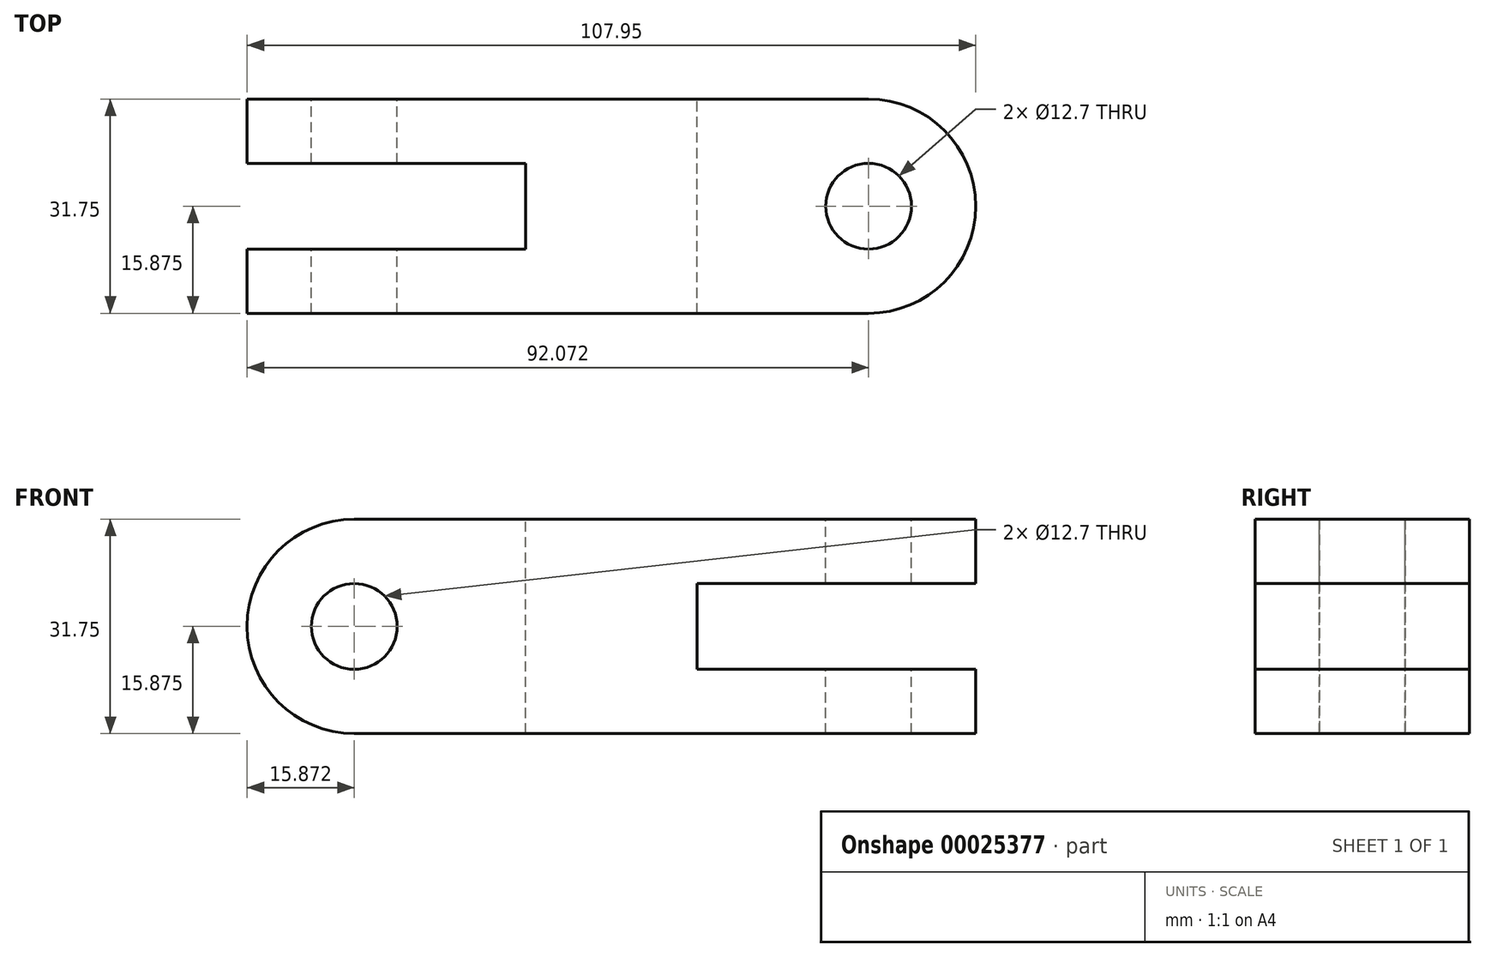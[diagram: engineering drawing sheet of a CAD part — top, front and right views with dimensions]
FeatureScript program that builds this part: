
annotation { "Feature Type Name" : "Feature", "Feature Type Description" : "" }
export const myFeature = defineFeature(function(context is Context, id is Id, definition is map)
    precondition{}
    {
        {
            var Q0;
            Q0=qCreatedBy(makeId("Front.planeOp"),FACE);
            var sketch = newSketch(context, id + "F0", { "sketchPlane" : qUnion([Q0])});
            skLineSegment(sketch, "E0.bottom", {"start": v(-48.62, 38.86) * mm, "end": v(59.33, 38.86) * mm});
            skLineSegment(sketch, "E0.top", {"start": v(-48.62, 7.1) * mm, "end": v(59.33, 7.1) * mm});
            skLineSegment(sketch, "E0.left", {"start": v(-48.62, 38.86) * mm, "end": v(-48.62, 29.33) * mm});
            skLineSegment(sketch, "E0.right", {"start": v(59.33, 38.86) * mm, "end": v(59.33, 7.1) * mm});
            skLineSegment(sketch, "E1.0", {"start": v(-48.62, 29.33) * mm, "end": v(-47.3, 29.33) * mm});
            skLineSegment(sketch, "E2.0", {"start": v(-48.62, 16.63) * mm, "end": v(-47.3, 16.63) * mm});
            skLineSegment(sketch, "E3.0", {"start": v(18.05, 29.33) * mm, "end": v(18.05, 16.63) * mm});
            skArc(sketch, "E4", {"start": v(-32.75, 38.86) * mm, "mid": v(-48.62, 22.98) * mm, "end": v(-32.75, 7.1) * mm});
            skCircle(sketch, "E5", {"center": v(-32.75, 22.98) * mm, "radius": 6.35 * mm});
            skLineSegment(sketch, "E6.trimOffspring", {"start": v(18.05, 29.33) * mm, "end": v(59.33, 29.33) * mm});
            skLineSegment(sketch, "E7.trimOffspring", {"start": v(18.05, 16.63) * mm, "end": v(59.33, 16.63) * mm});
            skLineSegment(sketch, "E8.trimOffspring", {"start": v(-48.62, 16.63) * mm, "end": v(-48.62, 7.1) * mm});
            skSolve(sketch);
        }
        {
            var Q0;
            Q0=makeQuery(id+"F0.imprint","IMPRINT",FACE,{"disambiguationData":[TD([[makeQuery(id+"F0.imprint","IMPRINT",EDGE,{"derivedFrom":sQuery(id+"F0.wireOp",EDGE,"E3.0")}),-1.0]])]});
            extrude(context, id + "F1", {"entities" : qUnion([Q0]), "depth" : 31.75 * mm});
        }
        {
            var Q0;
            Q0=makeQuery(id+"F0.imprint","IMPRINT",FACE,{"disambiguationData":[TD([[makeQuery(id+"F0.imprint","IMPRINT",EDGE,{"derivedFrom":sQuery(id+"F0.wireOp",EDGE,"E3.0")}),-1.0]])]});
            extrude(context, id + "F2", {"entities" : qUnion([Q0]), "operationType" : NewBodyOperationType.REMOVE, "endBound" : BoundingType.THROUGH_ALL, "oppositeDirection" : true, "depth" : 25.4 * mm});
        }
        {
            var Q0;
            Q0=makeQuery(id+"F1.opExtrude","SWEPT_FACE",FACE,{"disambiguationData":[OSD([sQuery(id+"F0.wireOp",EDGE,"E0.bottom")])]});
            var sketch = newSketch(context, id + "F3", { "sketchPlane" : qUnion([Q0])});
            skLineSegment(sketch, "E9.0", {"start": v(-48.62, -31.75) * mm, "end": v(-48.62, 0) * mm});
            skLineSegment(sketch, "E10", {"start": v(-48.62, 0) * mm, "end": v(59.33, 0) * mm});
            skLineSegment(sketch, "E11", {"start": v(-48.62, -31.75) * mm, "end": v(59.33, -31.75) * mm});
            skLineSegment(sketch, "E12.0", {"start": v(-48.62, -9.53) * mm, "end": v(-7.35, -9.53) * mm});
            skLineSegment(sketch, "E13.0", {"start": v(-48.62, -22.23) * mm, "end": v(-7.35, -22.23) * mm});
            skLineSegment(sketch, "E14.0", {"start": v(-7.35, -22.23) * mm, "end": v(-7.35, -9.52) * mm});
            skCircle(sketch, "E15", {"center": v(43.45, -15.88) * mm, "radius": 6.35 * mm});
            skPoint(sketch, "E16.orphan", {"position": v(43.45, 0) * mm});
            skPoint(sketch, "E17.start.orphan", {"position": v(43.45, -31.75) * mm});
            skCircle(sketch, "E18", {"center": v(43.45, -15.88) * mm, "radius": 15.88 * mm});
            skSolve(sketch);
        }
        {
            var Q0;
            {var subQ3=sQuery(id+"F3.wireOp",EDGE,"E12.0");var subQ5=sQuery(id+"F3.wireOp",EDGE,"E9.0");var subQ7=makeQuery(id+"F3.imprint","INTERSECT",VERTEX,{"derivedFrom":[subQ5,subQ3]});Q0=makeQuery(id+"F3.imprint","IMPRINT",FACE,{"disambiguationData":[TD([[makeQuery(id+"F3.imprint","IMPRINT",EDGE,{"disambiguationData":[TD([[subQ7,1.0]])],"derivedFrom":subQ5}),-1.0]])]});}
            var Q1;
            {var subQ5=sQuery(id+"F3.wireOp",EDGE,"E14.0");Q1=makeQuery(id+"F3.imprint","IMPRINT",FACE,{"disambiguationData":[TD([[makeQuery(id+"F3.imprint","IMPRINT",EDGE,{"derivedFrom":subQ5}),1.0]])]});}
            var Q2;
            Q2=makeQuery(id+"F3.imprint","IMPRINT",FACE,{"disambiguationData":[TD([[makeQuery(id+"F3.imprint","IMPRINT",EDGE,{"derivedFrom":sQuery(id+"F3.wireOp",EDGE,"E15")}),1.0]])]});
            var Q3;
            {var subQ0=sQuery(id+"F3.wireOp",EDGE,"E18");var subQ3=sQuery(id+"F3.wireOp",EDGE,"E10");var subQ4=makeQuery(id+"F3.imprint","INTERSECT",VERTEX,{"derivedFrom":[subQ3,subQ0]});Q3=makeQuery(id+"F3.imprint","IMPRINT",FACE,{"disambiguationData":[TD([[makeQuery(id+"F3.imprint","IMPRINT",EDGE,{"disambiguationData":[TD([[subQ4,-1.0]])],"derivedFrom":subQ3}),-1.0]])]});}
            var Q4;
            {var subQ1=sQuery(id+"F3.wireOp",EDGE,"E18");var subQ3=sQuery(id+"F3.wireOp",EDGE,"E11");var subQ5=makeQuery(id+"F3.imprint","INTERSECT",VERTEX,{"derivedFrom":[subQ3,subQ1]});Q4=makeQuery(id+"F3.imprint","IMPRINT",FACE,{"disambiguationData":[TD([[makeQuery(id+"F3.imprint","IMPRINT",EDGE,{"disambiguationData":[TD([[subQ5,-1.0]])],"derivedFrom":subQ3}),1.0]])]});}
            extrude(context, id + "F4", {"entities" : qUnion([Q0, Q1, Q2, Q3, Q4]), "operationType" : NewBodyOperationType.REMOVE, "endBound" : BoundingType.THROUGH_ALL, "oppositeDirection" : true, "depth" : 25.4 * mm});
        }
    });
